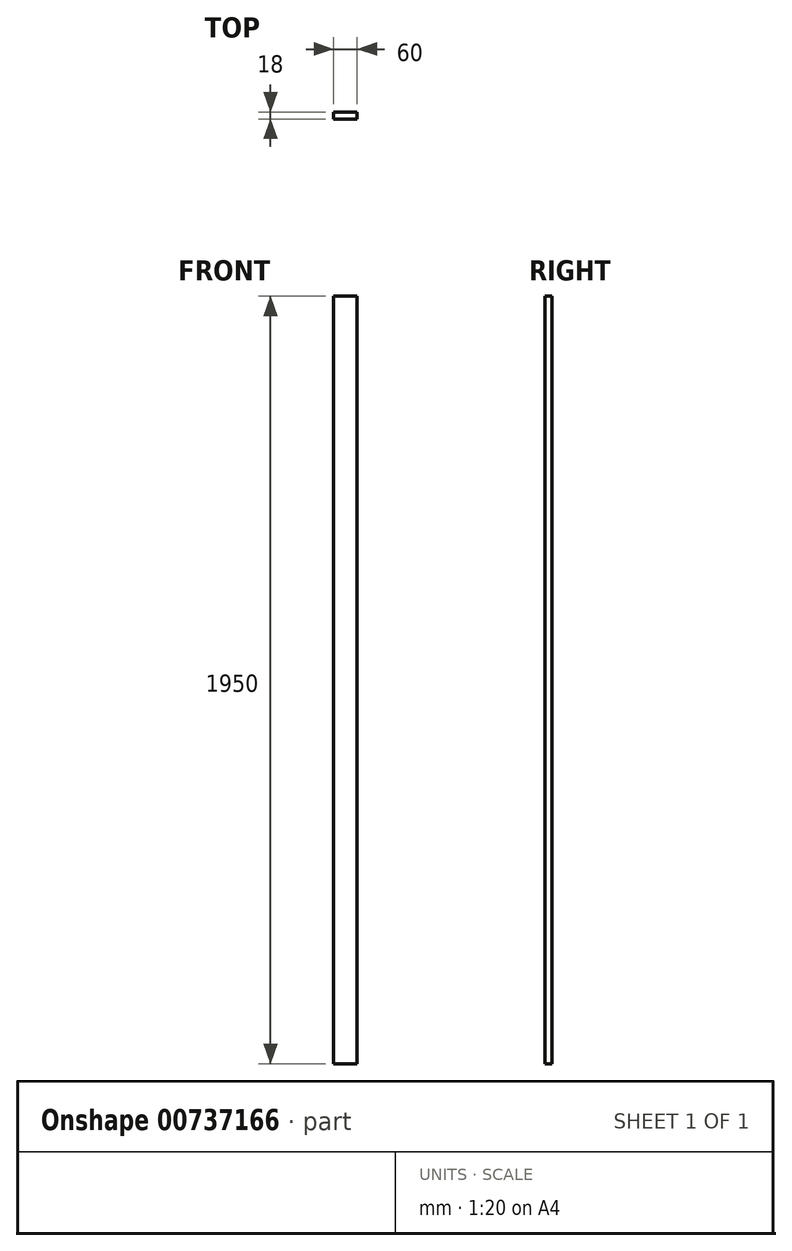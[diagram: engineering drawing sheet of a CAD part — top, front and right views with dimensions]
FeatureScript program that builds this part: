
annotation { "Feature Type Name" : "Feature", "Feature Type Description" : "" }
export const myFeature = defineFeature(function(context is Context, id is Id, definition is map)
    precondition{}
    {
        {
            var Q0;
            Q0=qCreatedBy(makeId("Front.planeOp"),FACE);
            var sketch = newSketch(context, id + "F0", { "sketchPlane" : qUnion([Q0])});
            skLineSegment(sketch, "E0.bottom", {"start": v(30, 975) * mm, "end": v(-30, 975) * mm});
            skLineSegment(sketch, "E0.top", {"start": v(30, -975) * mm, "end": v(-30, -975) * mm});
            skLineSegment(sketch, "E0.left", {"start": v(30, 975) * mm, "end": v(30, -975) * mm});
            skLineSegment(sketch, "E0.right", {"start": v(-30, 975) * mm, "end": v(-30, -975) * mm});
            skPoint(sketch, "E0.middle", {"position": v(0, 0) * mm});
            skSolve(sketch);
        }
        {
            var Q0;
            Q0 = qSketchRegion(id + "F0", true);
            extrude(context, id + "F1", {"entities" : qUnion([Q0]), "endBound" : BoundingType.SYMMETRIC, "depth" : 18 * mm, "offsetDistance" : 25 * mm});
        }
    });
